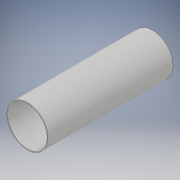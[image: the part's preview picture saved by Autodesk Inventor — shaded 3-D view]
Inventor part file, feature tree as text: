
AUTODESK INVENTOR PART (.ipt)
format: ipt  version: 2019 (Build 230136000, 136)  size: 99,328 bytes
history: native  units: mm
features: extrude x2, sketch x2
ambient origin geometry x8: Origin, YZ Plane, XZ Plane, XY Plane, X Axis, Y Axis, Z Axis, Center Point
bodies: Solid1 (feature_tree)
feature tree (4):
  extrude  "Extrusion1"  Depth=540.0mm TaperAngle=0.0deg
  extrude  "Extrusion2"  Depth=54.0mm TaperAngle=0.0deg
  sketch  "Sketch1"  dims[d0=177.2mm d1=540.0mm d2=0.0mm]
  sketch  "Sketch2"  dims[d3=170.3mm d4=54.0mm d5=0.0mm]
